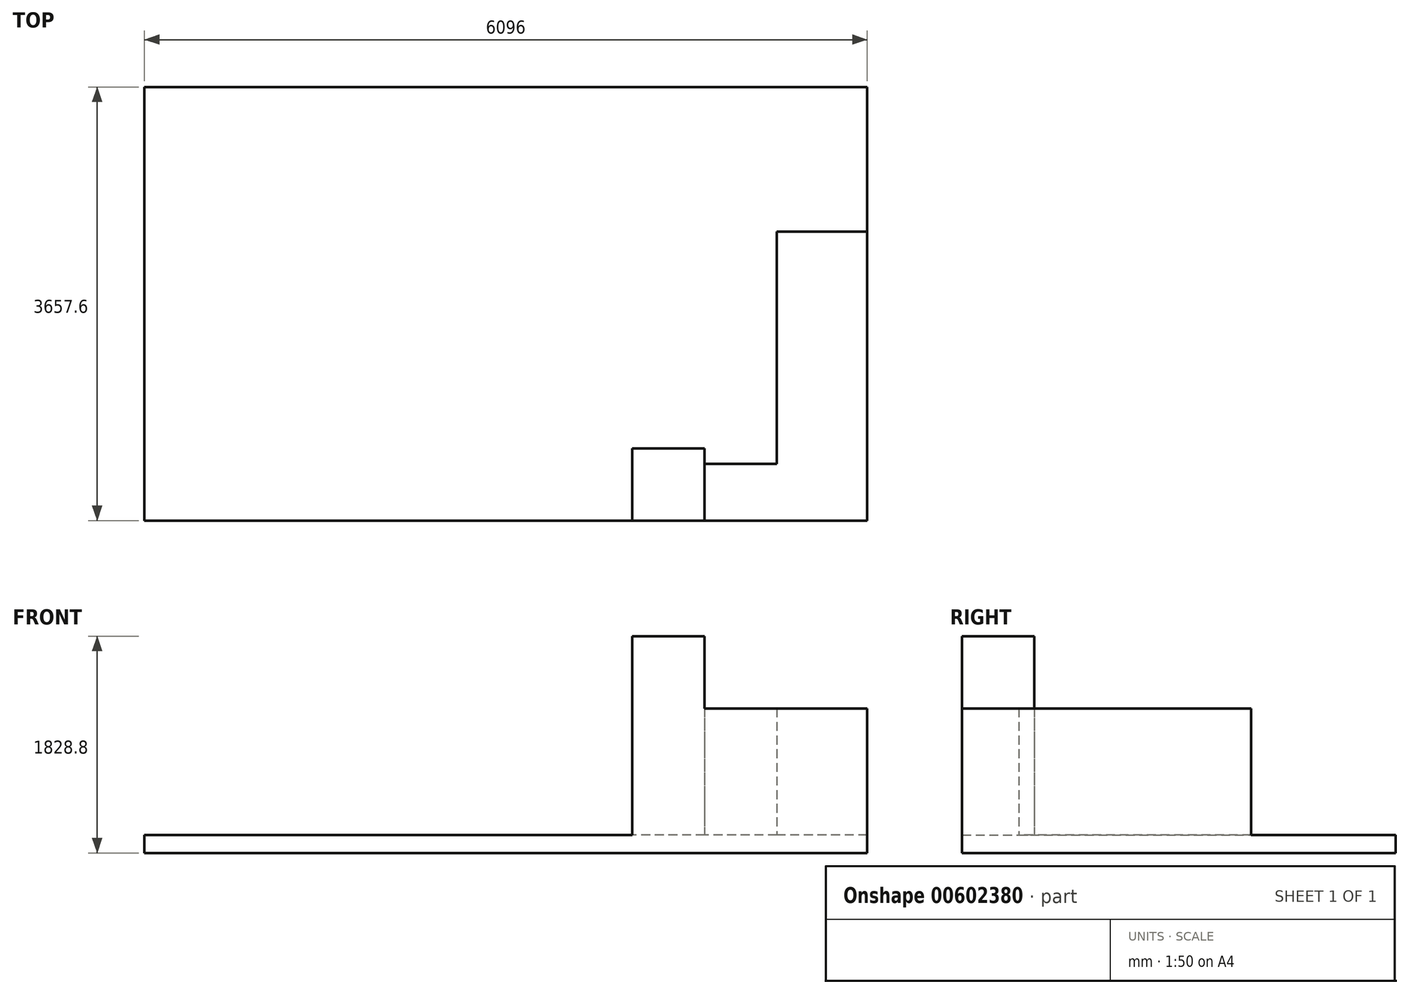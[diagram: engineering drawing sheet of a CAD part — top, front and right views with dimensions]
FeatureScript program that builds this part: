
annotation { "Feature Type Name" : "Feature", "Feature Type Description" : "" }
export const myFeature = defineFeature(function(context is Context, id is Id, definition is map)
    precondition{}
    {
        {
            var Q0;
            Q0=qCreatedBy(makeId("Top.planeOp"),FACE);
            var sketch = newSketch(context, id + "F0", { "sketchPlane" : qUnion([Q0])});
            skLineSegment(sketch, "E0.bottom", {"start": v(-44.75, -28.06) * mm, "end": v(6051.25, -28.06) * mm});
            skLineSegment(sketch, "E0.top", {"start": v(-44.75, 3629.54) * mm, "end": v(6051.25, 3629.54) * mm});
            skLineSegment(sketch, "E0.left", {"start": v(-44.75, -28.06) * mm, "end": v(-44.75, 3629.54) * mm});
            skLineSegment(sketch, "E0.right", {"start": v(6051.25, -28.06) * mm, "end": v(6051.25, 3629.54) * mm});
            skSolve(sketch);
        }
        {
            var Q0;
            Q0=makeQuery(id+"F0.imprint","IMPRINT",FACE,{"disambiguationData":[TD([[makeQuery(id+"F0.imprint","IMPRINT",EDGE,{"derivedFrom":sQuery(id+"F0.wireOp",EDGE,"E0.bottom")}),1.0]])]});
            extrude(context, id + "F1", {"entities" : qUnion([Q0]), "oppositeDirection" : true, "depth" : 152.4 * mm, "offsetDistance" : 25 * mm});
        }
        {
            var Q0;
            Q0=makeQuery(id+"F1.opExtrude","CAP_FACE",FACE,{"disambiguationData":[OSD([sQuery(id+"F0.wireOp",EDGE,"E0.bottom"),sQuery(id+"F0.wireOp",EDGE,"E0.top"),sQuery(id+"F0.wireOp",EDGE,"E0.left"),sQuery(id+"F0.wireOp",EDGE,"E0.right")])],"isStart":true});
            var sketch = newSketch(context, id + "F2", { "sketchPlane" : qUnion([Q0])});
            skLineSegment(sketch, "E1.bottom", {"start": v(6051.25, 3629.54) * mm, "end": v(4527.25, 3629.54) * mm});
            skLineSegment(sketch, "E1.top", {"start": v(6051.25, 2410.34) * mm, "end": v(4527.25, 2410.34) * mm});
            skLineSegment(sketch, "E1.left", {"start": v(6051.25, 3629.54) * mm, "end": v(6051.25, 2410.34) * mm});
            skLineSegment(sketch, "E1.right", {"start": v(4527.25, 3629.54) * mm, "end": v(4527.25, 2410.34) * mm});
            skLineSegment(sketch, "E2.top", {"start": v(6051.25, -28.06) * mm, "end": v(5289.25, -28.06) * mm});
            skLineSegment(sketch, "E2.left", {"start": v(6051.25, 2410.34) * mm, "end": v(6051.25, -28.06) * mm});
            skLineSegment(sketch, "E2.right", {"start": v(5289.25, 2410.34) * mm, "end": v(5289.25, -28.06) * mm});
            skLineSegment(sketch, "E3.bottom", {"start": v(5289.25, -28.06) * mm, "end": v(4679.65, -28.06) * mm});
            skLineSegment(sketch, "E3.top", {"start": v(5289.25, 450.5) * mm, "end": v(4679.65, 450.5) * mm});
            skLineSegment(sketch, "E3.left", {"start": v(5289.25, -28.06) * mm, "end": v(5289.25, 450.5) * mm});
            skLineSegment(sketch, "E3.right", {"start": v(4679.65, -28.06) * mm, "end": v(4679.65, 450.5) * mm});
            skLineSegment(sketch, "E4.bottom", {"start": v(4679.65, -28.06) * mm, "end": v(4070.05, -28.06) * mm});
            skLineSegment(sketch, "E4.top", {"start": v(4679.65, 581.54) * mm, "end": v(4070.05, 581.54) * mm});
            skLineSegment(sketch, "E4.left", {"start": v(4679.65, -28.06) * mm, "end": v(4679.65, 581.54) * mm});
            skLineSegment(sketch, "E4.right", {"start": v(4070.05, -28.06) * mm, "end": v(4070.05, 581.54) * mm});
            skSolve(sketch);
        }
        {
            var Q0;
            Q0=makeQuery(id+"F2.imprint","IMPRINT",FACE,{"disambiguationData":[TD([[makeQuery(id+"F2.imprint","IMPRINT",EDGE,{"derivedFrom":sQuery(id+"F2.wireOp",EDGE,"E2.top")}),1.0]])]});
            var Q1;
            {var subQ0=sQuery(id+"F2.wireOp",EDGE,"E3.bottom");Q1=makeQuery(id+"F2.imprint","IMPRINT",FACE,{"disambiguationData":[TD([[makeQuery(id+"F2.imprint","IMPRINT",EDGE,{"derivedFrom":subQ0}),1.0]])]});}
            extrude(context, id + "F3", {"entities" : qUnion([Q0, Q1]), "operationType" : NewBodyOperationType.ADD, "depth" : 1066.8 * mm, "offsetDistance" : 30.48 * mm});
        }
        {
            var Q0;
            {var subQ3=sQuery(id+"F2.wireOp",EDGE,"E4.bottom");Q0=makeQuery(id+"F2.imprint","IMPRINT",FACE,{"disambiguationData":[TD([[makeQuery(id+"F2.imprint","IMPRINT",EDGE,{"derivedFrom":subQ3}),1.0]])]});}
            extrude(context, id + "F4", {"entities" : qUnion([Q0]), "operationType" : NewBodyOperationType.ADD, "depth" : 1676.4 * mm, "offsetDistance" : 30.48 * mm});
        }
    });
